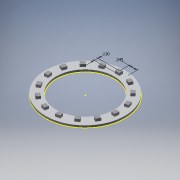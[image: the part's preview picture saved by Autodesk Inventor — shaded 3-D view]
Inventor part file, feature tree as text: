
AUTODESK INVENTOR PART (.ipt)
format: ipt  version: 2017 (Build 210142000, 142)  size: 215,040 bytes
history: native  units: in
note: dims shown in document units (in); Inventor stores cm internally (conversion verified against a paired STEP export)
features: sketch x4, extrude x2, revolve x2, pattern_circular x1, plane x1, projected_geometry x1
ambient origin geometry x8: Origin, YZ Plane, XZ Plane, XY Plane, X Axis, Y Axis, Z Axis, Center Point
bodies: Solid1 (feature_tree)
feature tree (11):
  extrude  "Extrusion1"  Depth=1.725in
  extrude  "Extrusion2"  Depth=0.13in
  pattern_circular  "Circular Pattern1"  Count=15 Angle=360.0deg
  revolve  "Revolution1"  [1 undecoded]
  plane  "Work Plane1"
  revolve  "Revolution2"  [1 undecoded]
  sketch  "Sketch1"  dims[d0=2.36in d1=1.725in]
  sketch  "Sketch2"  dims[d2=0.06in d3=0.0in d4=0.13in]
  sketch  "Sketch4"  dims[d5=0.1102in]
  sketch  "Sketch5"  dims[d7=0.0748in d8=0.0in d9=5.9055in d10=360.0deg d12=0.9525in d21=0.125in d22=0.012in d23=0.1in d24=90.0deg d25=0.05in d26=0.0147in d27=0.285in d28=0.0344in]
  projected_geometry  "Projected Loop1"
note: 2 required parameter values undecoded (feature->parameter linkage not recoverable at this tier; creation-order binding heuristic only, values carry confidence <= 0.55)
